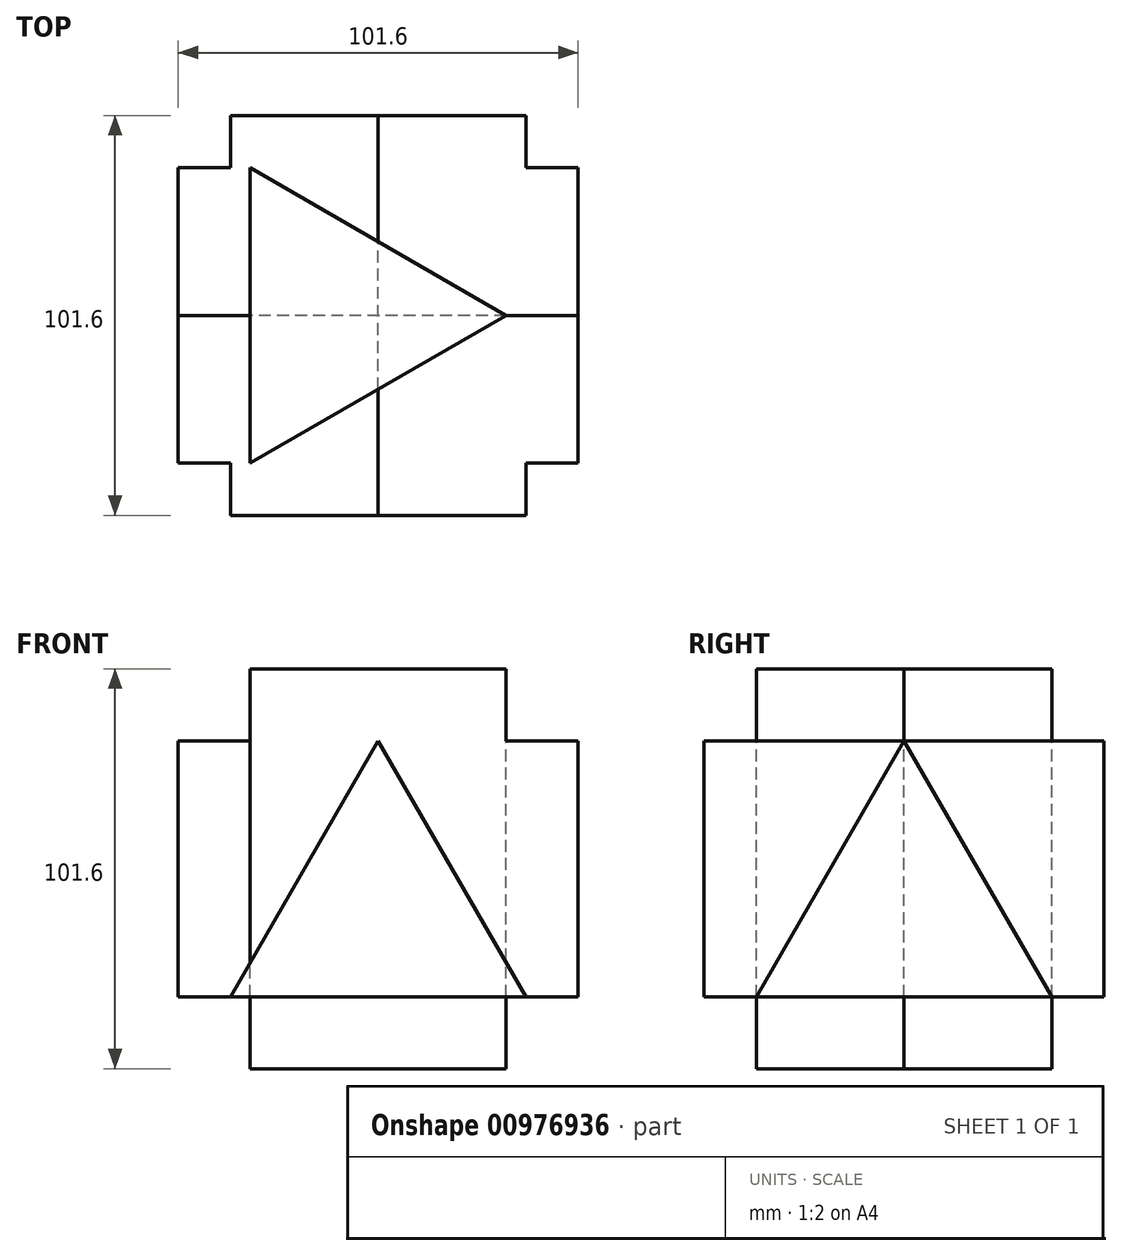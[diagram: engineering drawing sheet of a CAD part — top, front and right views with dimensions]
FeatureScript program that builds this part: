
annotation { "Feature Type Name" : "Feature", "Feature Type Description" : "" }
export const myFeature = defineFeature(function(context is Context, id is Id, definition is map)
    precondition{}
    {
        {
            var Q0;
            Q0=qCreatedBy(makeId("Right.planeOp"),FACE);
            var sketch = newSketch(context, id + "F0", { "sketchPlane" : qUnion([Q0])});
            skCircle(sketch, "E0.cCircle", {"center": v(-6.46, 6.37) * mm, "radius": 21.67 * mm, "construction": true});
            skLineSegment(sketch, "E0.0", {"start": v(31.07, -15.3) * mm, "end": v(-43.98, -15.3) * mm});
            skLineSegment(sketch, "E0.1", {"start": v(-43.98, -15.3) * mm, "end": v(-6.46, 49.7) * mm});
            skLineSegment(sketch, "E0.2", {"start": v(-6.46, 49.7) * mm, "end": v(31.07, -15.3) * mm});
            skPoint(sketch, "E0.0.midPoint", {"position": v(-6.46, -15.3) * mm});
            skLineSegment(sketch, "E1", {"start": v(-6.46, 49.7) * mm, "end": v(-6.46, -15.3) * mm});
            skLineSegment(sketch, "E2", {"start": v(-6.46, -15.3) * mm, "end": v(-6.46, 17.2) * mm});
            skLineSegment(sketch, "E3", {"start": v(-6.46, 17.2) * mm, "end": v(-25.22, 17.2) * mm});
            skLineSegment(sketch, "E4", {"start": v(-25.22, 17.2) * mm, "end": v(12.3, 17.2) * mm});
            skSolve(sketch);
        }
        {
            var Q0;
            {var subQ1=sQuery(id+"F0.wireOp",EDGE,"E0.1");var subQ3=sQuery(id+"F0.wireOp",EDGE,"YC9kPDgF-Arxk-NpA4-P3xO-IQXJig02Tubs");var subQ4=makeQuery(id+"F0.imprint","INTERSECT",VERTEX,{"derivedFrom":[subQ1,subQ3]});Q0=makeQuery(id+"F0.imprint","IMPRINT",FACE,{"disambiguationData":[TD([[makeQuery(id+"F0.imprint","IMPRINT",EDGE,{"disambiguationData":[TD([[subQ4,1.0]])],"derivedFrom":subQ3}),-1.0]])]});}
            var Q1;
            {var subQ1=sQuery(id+"F0.wireOp",EDGE,"E0.2");var subQ3=sQuery(id+"F0.wireOp",EDGE,"YC9kPDgF-Arxk-NpA4-P3xO-IQXJig02Tubs");var subQ4=makeQuery(id+"F0.imprint","INTERSECT",VERTEX,{"derivedFrom":[subQ1,subQ3]});Q1=makeQuery(id+"F0.imprint","IMPRINT",FACE,{"disambiguationData":[TD([[makeQuery(id+"F0.imprint","IMPRINT",EDGE,{"disambiguationData":[TD([[subQ4,-1.0]])],"derivedFrom":subQ3}),-1.0]])]});}
            var Q2;
            {var subQ0=sQuery(id+"F0.wireOp",EDGE,"E0.2");var subQ1=sQuery(id+"F0.wireOp",EDGE,"E0.0");var subQ2=makeQuery(id+"F0.imprint","INTERSECT",VERTEX,{"derivedFrom":[subQ1,subQ0]});Q2=makeQuery(id+"F0.imprint","IMPRINT",FACE,{"disambiguationData":[TD([[makeQuery(id+"F0.imprint","IMPRINT",EDGE,{"disambiguationData":[TD([[subQ2,-1.0]])],"derivedFrom":subQ1}),-1.0]])]});}
            var Q3;
            {var subQ0=sQuery(id+"F0.wireOp",EDGE,"E0.1");var subQ1=sQuery(id+"F0.wireOp",EDGE,"E0.0");var subQ2=makeQuery(id+"F0.imprint","INTERSECT",VERTEX,{"derivedFrom":[subQ1,subQ0]});Q3=makeQuery(id+"F0.imprint","IMPRINT",FACE,{"disambiguationData":[TD([[makeQuery(id+"F0.imprint","IMPRINT",EDGE,{"disambiguationData":[TD([[subQ2,1.0]])],"derivedFrom":subQ1}),-1.0]])]});}
            var Q4;
            {var subQ0=sQuery(id+"F0.wireOp",EDGE,"E1");Q4=makeQuery(id+"F0.imprint","IMPRINT",FACE,{"disambiguationData":[TD([[makeQuery(id+"F0.imprint","IMPRINT",EDGE,{"derivedFrom":subQ0}),-1.0]])]});}
            var Q5;
            {var subQ0=sQuery(id+"F0.wireOp",EDGE,"E1");Q5=makeQuery(id+"F0.imprint","IMPRINT",FACE,{"disambiguationData":[TD([[makeQuery(id+"F0.imprint","IMPRINT",EDGE,{"derivedFrom":subQ0}),1.0]])]});}
            extrude(context, id + "F1", {"entities" : qUnion([Q0, Q1, Q2, Q3, Q4, Q5]), "depth" : 50.8 * mm, "offsetDistance" : 25.4 * mm});
        }
        {
            var Q0;
            Q0=makeQuery(id+"F1.opExtrude","CAP_FACE",FACE,{"disambiguationData":[OSD([sQuery(id+"F0.wireOp",EDGE,"E0.0"),sQuery(id+"F0.wireOp",EDGE,"E0.1"),sQuery(id+"F0.wireOp",EDGE,"E0.2")])],"isStart":true});
            extrude(context, id + "F2", {"entities" : qUnion([Q0]), "operationType" : NewBodyOperationType.ADD, "depth" : 50.8 * mm, "offsetDistance" : 25.4 * mm});
        }
        {
            var Q0;
            Q0=makeQuery(id+"F1.opExtrude","SWEPT_BODY",BODY,{"disambiguationData":[OSD([sQuery(id+"F0.wireOp",EDGE,"E0.0"),sQuery(id+"F0.wireOp",EDGE,"E0.1"),sQuery(id+"F0.wireOp",EDGE,"E0.2")])]});
            var Q1;
            Q1=sQuery(id+"F0.wireOp",EDGE,"E4");
            circularPattern(context, id + "F3", {"entities" : qUnion([Q0]), "axis" : qUnion([Q1]), "angle" : 90 * degree, "instanceCount" : 2, "equalSpace" : true});
        }
        {
            var Q0;
            Q0=makeQuery(id+"F1.opExtrude","SWEPT_BODY",BODY,{"disambiguationData":[OSD([sQuery(id+"F0.wireOp",EDGE,"E0.0"),sQuery(id+"F0.wireOp",EDGE,"E0.1"),sQuery(id+"F0.wireOp",EDGE,"E0.2")])]});
            var Q1;
            Q1=sQuery(id+"F0.wireOp",EDGE,"E1");
            circularPattern(context, id + "F4", {"entities" : qUnion([Q0]), "axis" : qUnion([Q1]), "angle" : 90 * degree, "instanceCount" : 2, "equalSpace" : true});
        }
    });
